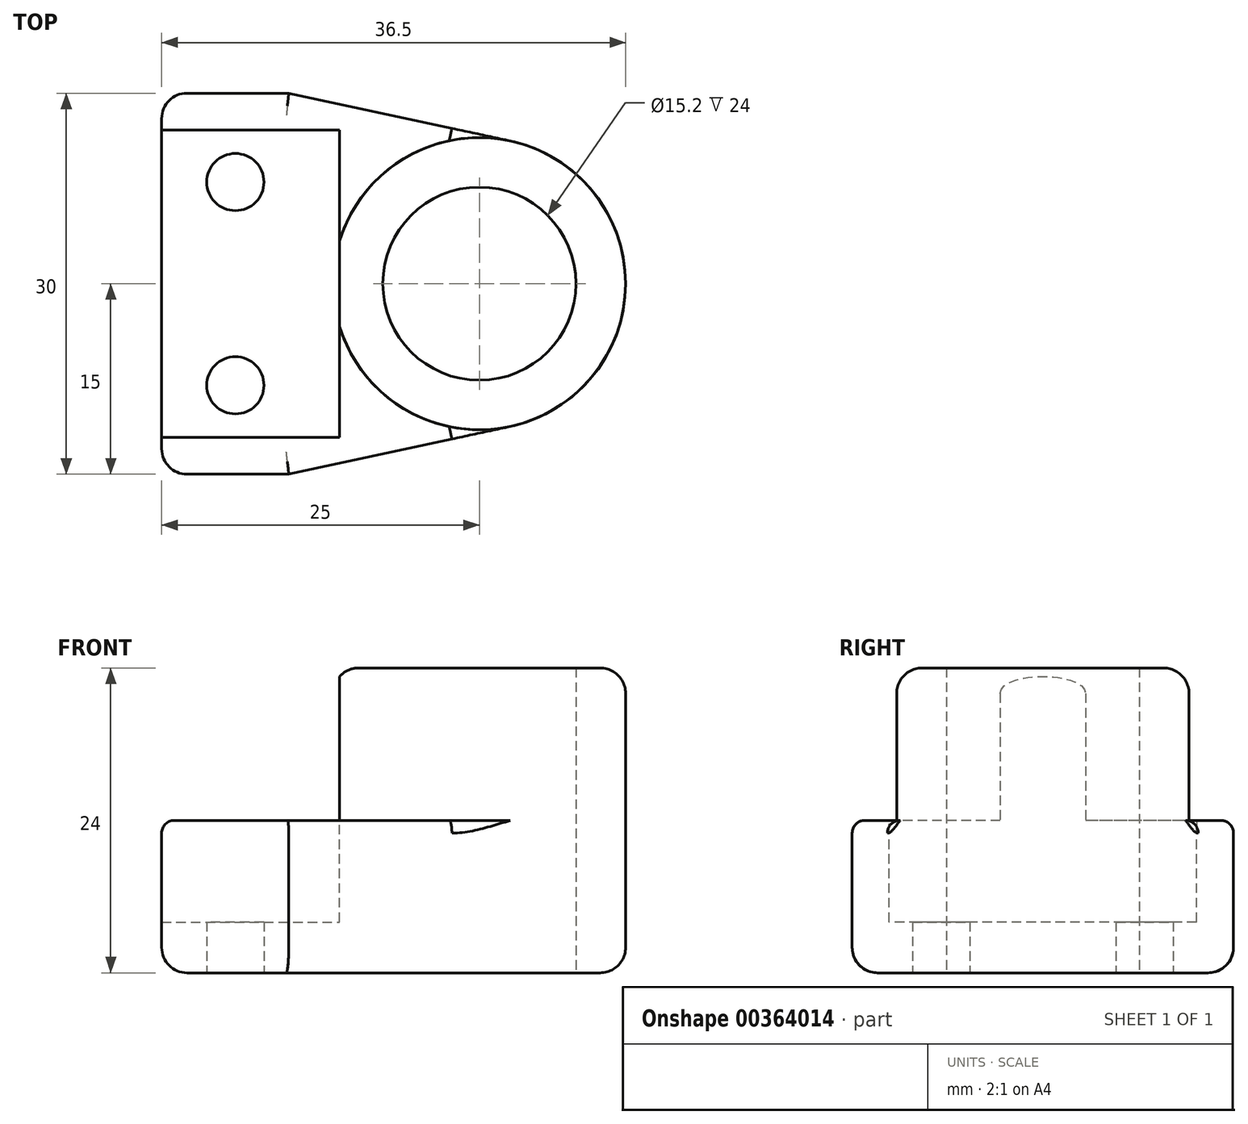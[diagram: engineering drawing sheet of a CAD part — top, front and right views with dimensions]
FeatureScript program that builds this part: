
annotation { "Feature Type Name" : "Feature", "Feature Type Description" : "" }
export const myFeature = defineFeature(function(context is Context, id is Id, definition is map)
    precondition{}
    {
        {
            var Q0;
            Q0=qCreatedBy(makeId("Top.planeOp"),FACE);
            var sketch = newSketch(context, id + "F0", { "sketchPlane" : qUnion([Q0])});
            skCircle(sketch, "E0", {"center": v(0, 0) * mm, "radius": 7.6 * mm});
            skArc(sketch, "E1", {"start": v(2.42, 11.24) * mm, "mid": v(11.5, 0) * mm, "end": v(2.42, -11.24) * mm});
            skLineSegment(sketch, "E2", {"start": v(-15, 15) * mm, "end": v(2.42, 11.24) * mm});
            skLineSegment(sketch, "E3", {"start": v(-15, -15) * mm, "end": v(2.42, -11.24) * mm});
            skLineSegment(sketch, "E4", {"start": v(-15, 15) * mm, "end": v(-25, 15) * mm});
            skLineSegment(sketch, "E5", {"start": v(-25, 15) * mm, "end": v(-25, -15) * mm});
            skLineSegment(sketch, "E6", {"start": v(-25, -15) * mm, "end": v(-15, -15) * mm});
            skLineSegment(sketch, "E7", {"start": v(-11, 9.97) * mm, "end": v(-11, -5.84) * mm, "construction": true});
            skCircle(sketch, "E8", {"center": v(-19.2, 8) * mm, "radius": 2.25 * mm});
            skCircle(sketch, "E9.MirrorC", {"center": v(-19.2, -8) * mm, "radius": 2.25 * mm});
            skSolve(sketch);
        }
        {
            var Q0;
            Q0 = qSketchRegion(id + "F0", true);
            extrude(context, id + "F1", {"entities" : qUnion([Q0]), "depth" : 12 * mm});
        }
        {
            var Q0;
            Q0=makeQuery(id+"F1.opExtrude","CAP_FACE",FACE,{"disambiguationData":[OSD([sQuery(id+"F0.wireOp",EDGE,"E0"),sQuery(id+"F0.wireOp",EDGE,"E1"),sQuery(id+"F0.wireOp",EDGE,"E2"),sQuery(id+"F0.wireOp",EDGE,"E3"),sQuery(id+"F0.wireOp",EDGE,"E4"),sQuery(id+"F0.wireOp",EDGE,"E5"),sQuery(id+"F0.wireOp",EDGE,"E6")])],"isStart":false});
            var sketch = newSketch(context, id + "F2", { "sketchPlane" : qUnion([Q0])});
            skLineSegment(sketch, "E10", {"start": v(-25, -12.1) * mm, "end": v(-25, 12.1) * mm});
            skLineSegment(sketch, "E11", {"start": v(-25, 12.1) * mm, "end": v(-11, 12.1) * mm});
            skLineSegment(sketch, "E12", {"start": v(-11, 12.1) * mm, "end": v(-11, -12.1) * mm});
            skLineSegment(sketch, "E13", {"start": v(-11, -12.1) * mm, "end": v(-25, -12.1) * mm});
            skSolve(sketch);
        }
        {
            var Q0;
            Q0 = qSketchRegion(id + "F2", true);
            extrude(context, id + "F3", {"entities" : qUnion([Q0]), "operationType" : NewBodyOperationType.REMOVE, "oppositeDirection" : true, "depth" : 8 * mm});
        }
        {
            var Q0;
            Q0=makeQuery(id+"F1.opExtrude","CAP_FACE",FACE,{"disambiguationData":[OSD([sQuery(id+"F0.wireOp",EDGE,"E0"),sQuery(id+"F0.wireOp",EDGE,"E1"),sQuery(id+"F0.wireOp",EDGE,"E2"),sQuery(id+"F0.wireOp",EDGE,"E3"),sQuery(id+"F0.wireOp",EDGE,"E4"),sQuery(id+"F0.wireOp",EDGE,"E5"),sQuery(id+"F0.wireOp",EDGE,"E6"),sQuery(id+"F0.wireOp",EDGE,"E8"),sQuery(id+"F0.wireOp",EDGE,"E9.MirrorC")])],"isStart":false});
            var sketch = newSketch(context, id + "F4", { "sketchPlane" : qUnion([Q0])});
            skCircle(sketch, "E14", {"center": v(0, 0) * mm, "radius": 7.6 * mm});
            skArc(sketch, "E15", {"start": v(-11, 3.35) * mm, "mid": v(11.5, 0) * mm, "end": v(-11, -3.35) * mm});
            skLineSegment(sketch, "E16", {"start": v(-11, 3.35) * mm, "end": v(-11, -3.35) * mm});
            skSolve(sketch);
        }
        {
            var Q0;
            Q0 = qSketchRegion(id + "F4", true);
            extrude(context, id + "F5", {"entities" : qUnion([Q0]), "operationType" : NewBodyOperationType.ADD, "depth" : 12 * mm});
        }
        {
            var Q0;
            Q0=makeQuery(id+"F5.opExtrude","CAP_EDGE",EDGE,{"disambiguationData":[OSD([sQuery(id+"F4.wireOp",EDGE,"E15")])],"isStart":false});
            var Q1;
            Q1=makeQuery(id+"F1.opExtrude","CAP_EDGE",EDGE,{"disambiguationData":[OSD([sQuery(id+"F0.wireOp",EDGE,"E1")])],"isStart":true});
            var Q2;
            Q2=makeQuery(id+"F1.opExtrude","CAP_EDGE",EDGE,{"disambiguationData":[OSD([sQuery(id+"F0.wireOp",EDGE,"E5")])],"isStart":true});
            var Q3;
            Q3=makeQuery(id+"F1.opExtrude","CAP_EDGE",EDGE,{"disambiguationData":[OSD([sQuery(id+"F0.wireOp",EDGE,"E4")])],"isStart":true});
            var Q4;
            Q4=makeQuery(id+"F1.opExtrude","CAP_EDGE",EDGE,{"disambiguationData":[OSD([sQuery(id+"F0.wireOp",EDGE,"E6")])],"isStart":true});
            var Q5;
            Q5=makeQuery(id+"F1.opExtrude","SWEPT_EDGE",EDGE,{"disambiguationData":[OSD([sQuery(id+"F0.wireOp",EDGE,"E5"),sQuery(id+"F0.wireOp",EDGE,"E6")])]});
            var Q6;
            Q6=makeQuery(id+"F1.opExtrude","SWEPT_EDGE",EDGE,{"disambiguationData":[OSD([sQuery(id+"F0.wireOp",EDGE,"E4"),sQuery(id+"F0.wireOp",EDGE,"E5")])]});
            fillet(context, id + "F6", {"entities" : qUnion([Q0, Q1, Q2, Q3, Q4, Q5, Q6]), "radius" : 2 * mm, "tangentPropagation" : true, "allowEdgeOverflow" : false});
        }
        {
            var Q0;
            Q0=makeQuery(id+"F1.opExtrude","CAP_EDGE",EDGE,{"disambiguationData":[OSD([sQuery(id+"F0.wireOp",EDGE,"E4")])],"isStart":false});
            var Q1;
            Q1=makeQuery(id+"F1.opExtrude","CAP_EDGE",EDGE,{"disambiguationData":[OSD([sQuery(id+"F0.wireOp",EDGE,"E2")])],"isStart":false});
            var Q2;
            Q2=makeQuery(id+"F1.opExtrude","CAP_EDGE",EDGE,{"disambiguationData":[OSD([sQuery(id+"F0.wireOp",EDGE,"E3")])],"isStart":false});
            var Q3;
            Q3=makeQuery(id+"F1.opExtrude","CAP_EDGE",EDGE,{"disambiguationData":[OSD([sQuery(id+"F0.wireOp",EDGE,"E6")])],"isStart":false});
            fillet(context, id + "F7", {"entities" : qUnion([Q0, Q1, Q2, Q3]), "radius" : 1 * mm, "tangentPropagation" : true, "allowEdgeOverflow" : false});
        }
    });
